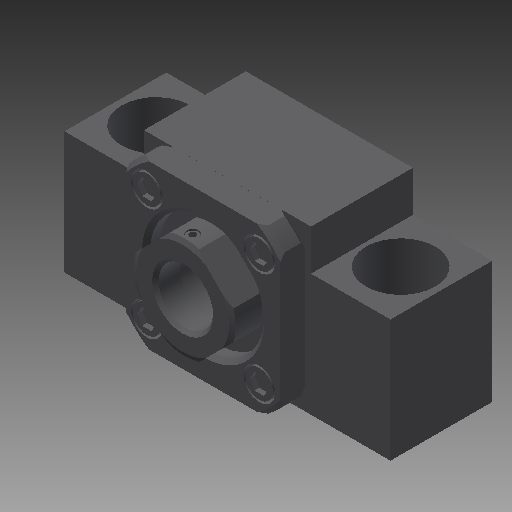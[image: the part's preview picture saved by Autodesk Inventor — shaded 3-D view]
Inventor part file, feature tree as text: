
AUTODESK INVENTOR PART (.ipt)
format: ipt  version: 2018 (Build 220112000, 112)  size: 392,704 bytes
history: native  units: mm
features: sketch x24, other x14, revolve x12, extrude x9, hole x3, pattern_linear x3, thread x1
ambient origin geometry x8: Origin, YZ Plane, XZ Plane, XY Plane, X Axis, Y Axis, Z Axis, Center Point
bodies: Solid1 (feature_tree)
feature tree (66):
  extrude  "Extrusion1"  Depth=2.5mm TaperAngle=0.0deg
  hole  "Hole1"  [1 undecoded]
  extrude  "Extrusion2"  TaperAngle=360.0deg  [1 undecoded]
  revolve  "Revolution1"  Angle=360.0deg
  extrude  "Extrusion3"  TaperAngle=360.0deg  [1 undecoded]
  extrude  "Extrusion4"  Depth=20.0mm
  revolve  "Revolution2"  [1 undecoded]
  hole  "Hole5"  [1 undecoded]
  revolve  "Revolution3"  Angle=360.0deg
  thread  "Thread1"  [1 undecoded]
  revolve  "Revolution4"  Angle=360.0deg
  revolve  "Revolution5"  [1 undecoded]
  pattern_linear  "Rectangular Pattern1"  Count1=8  [1 undecoded]
  revolve  "Revolution6"  [1 undecoded]
  pattern_linear  "Rectangular Pattern2"  Count1=4  [1 undecoded]
  extrude  "Extrusion5"  Depth=10.0mm
  pattern_linear  "Rectangular Pattern3"  Count1=2  [1 undecoded]
  revolve  "Revolution7"  [1 undecoded]
  revolve  "Revolution8"  [1 undecoded]
  extrude  "Extrusion6"  [1 undecoded]
  revolve  "Revolution9"  [1 undecoded]
  revolve  "Revolution10"  [1 undecoded]
  extrude  "Extrusion7"  [1 undecoded]
  extrude  "Extrusion8"  [1 undecoded]
  revolve  "Revolution11"  [1 undecoded]
  revolve  "Revolution12"  [1 undecoded]
  extrude  "Extrusion9"  [1 undecoded]
  other  "unit_XY"
  other  "unit_YZ"
  other  "unit_ZX"
  other  "unit_X"
  other  "unit_Y"
  other  "unit_Z"
  other  "unit_Center"
  other  "unit_collar_XY"
  other  "unit_collar_YZ"
  other  "unit_collar_ZX"
  other  "unit_collar_X"
  other  "unit_collar_Y"
  other  "unit_collar_Z"
  other  "unit_collar_Center"
  sketch  "Sketch_1"  dims[d0=25.0mm d1=0.0mm]
  sketch  "Sketch2"  dims[d2=11.0mm d3=6.0mm d4=17.0mm d5=15.0mm d6=90.0deg d7=38.0mm d8=0.0mm d30=2.5mm d31=0.0mm]
  sketch  "Sketch_10"  dims[d32=360.0deg d33=8.5mm d34=0.0mm]
  sketch  "Sketch_13"  dims[d49=360.0deg d50=20.0mm d52=27.577164mm d53=20.0mm d55=27.577164mm]
  sketch  "Sketch_11"  dims[d35=3.5mm d36=0.0mm d37=360.0deg]
  sketch  "Sketch_12"  dims[d46=6.876mm d47=0.0mm d48=360.0deg]
  sketch  "Sketch_14"  dims[d56=360.0deg d57=20.0mm d59=27.577164mm d60=20.0mm d62=27.577164mm]
  sketch  "Sketch11"  dims[d38=15.0mm d39=6.0mm d40=19.5mm d41=6.0mm d42=90.0deg d43=30.0mm d44=0.0mm d45=360.0deg]
  sketch  "Sketch_16"  dims[d63=1.2mm d64=0.0mm d65=20.0mm d67=27.577164mm d68=20.0mm d70=27.577164mm]
  sketch  "Sketch_17"  dims[d71=360.0deg d72=360.0deg d73=1.2mm d74=0.0mm]
  sketch  "Sketch_18"  dims[d75=360.0deg d76=360.0deg]
  sketch  "Sketch_20"  dims[d77=16.0mm d78=0.0mm d79=6.0mm d80=0.0mm]
  sketch  "Sketch_22"  dims[d81=360.0deg]
  sketch  "Sketch_24"  dims[d82=360.0deg]
  sketch  "Sketch_25"  dims[d83=0.01mm d84=0.0mm]
  sketch  "Sketch_26"  dims[d85=0.0mm]
  sketch  "Sketch_28"  dims[d91=28.0mm]
  sketch  "Sketch_29"  dims[d92=38.0mm]
  sketch  "Sketch_33"  dims[d101=0.0mm d102=90.0deg d103=15.0mm d104=17.0mm d105=38.0mm d106=11.0mm d107=10.0mm d108=10.0mm]
  sketch  "Sketch_27"  dims[d86=0.0mm d87=80.0mm]
  sketch  "Sketch_30"  dims[d93=38.0mm d94=40.0mm]
  sketch  "Sketch_31"  dims[d95=40.0mm d97=10.0mm d98=20.0mm]
  sketch  "Sketch_32"  dims[d99=6.0mm]
  sketch  "Sketch27"  dims[d88=40.0mm d90=41.0mm]
  hole  "Hole6"  [1 undecoded]
note: 22 required parameter values undecoded (feature->parameter linkage not recoverable at this tier; creation-order binding heuristic only, values carry confidence <= 0.55)